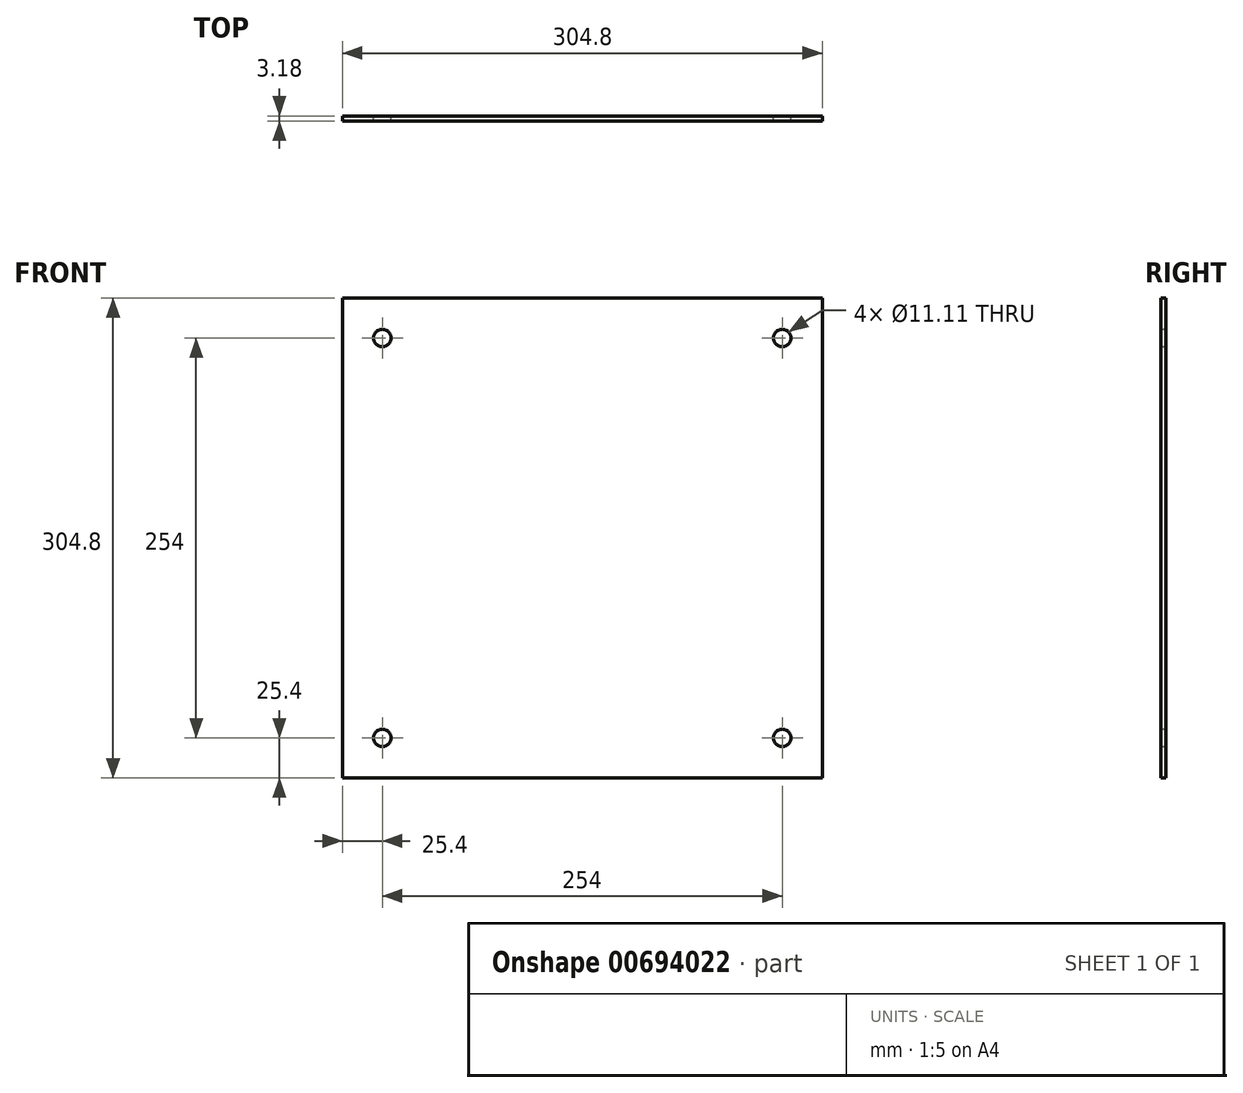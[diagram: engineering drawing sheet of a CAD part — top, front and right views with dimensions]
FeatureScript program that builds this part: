
annotation { "Feature Type Name" : "Feature", "Feature Type Description" : "" }
export const myFeature = defineFeature(function(context is Context, id is Id, definition is map)
    precondition{}
    {
        {
            var Q0;
            Q0=qCreatedBy(makeId("Front.planeOp"),FACE);
            var sketch = newSketch(context, id + "F0", { "sketchPlane" : qUnion([Q0])});
            skLineSegment(sketch, "E0.bottom", {"start": v(-152.4, 152.4) * mm, "end": v(152.4, 152.4) * mm});
            skLineSegment(sketch, "E0.top", {"start": v(-152.4, -152.4) * mm, "end": v(152.4, -152.4) * mm});
            skLineSegment(sketch, "E0.left", {"start": v(-152.4, 152.4) * mm, "end": v(-152.4, -152.4) * mm});
            skLineSegment(sketch, "E0.right", {"start": v(152.4, 152.4) * mm, "end": v(152.4, -152.4) * mm});
            skLineSegment(sketch, "E1", {"start": v(-152.4, 0) * mm, "end": v(152.4, 0) * mm, "construction": true});
            skCircle(sketch, "E2", {"center": v(-127, 127) * mm, "radius": 5.56 * mm});
            skCircle(sketch, "E3.MirrorC", {"center": v(127, 127) * mm, "radius": 5.56 * mm});
            skCircle(sketch, "E4.MirrorC", {"center": v(127, -127) * mm, "radius": 5.56 * mm});
            skCircle(sketch, "E5.MirrorC", {"center": v(-127, -127) * mm, "radius": 5.56 * mm});
            skSolve(sketch);
        }
        {
            var Q0;
            Q0=makeQuery(id+"F0.imprint","IMPRINT",FACE,{"disambiguationData":[TD([[makeQuery(id+"F0.imprint","IMPRINT",EDGE,{"derivedFrom":sQuery(id+"F0.wireOp",EDGE,"E0.bottom")}),-1.0]])]});
            extrude(context, id + "F1", {"entities" : qUnion([Q0]), "depth" : 3.17 * mm, "offsetDistance" : 25.4 * mm});
        }
    });
